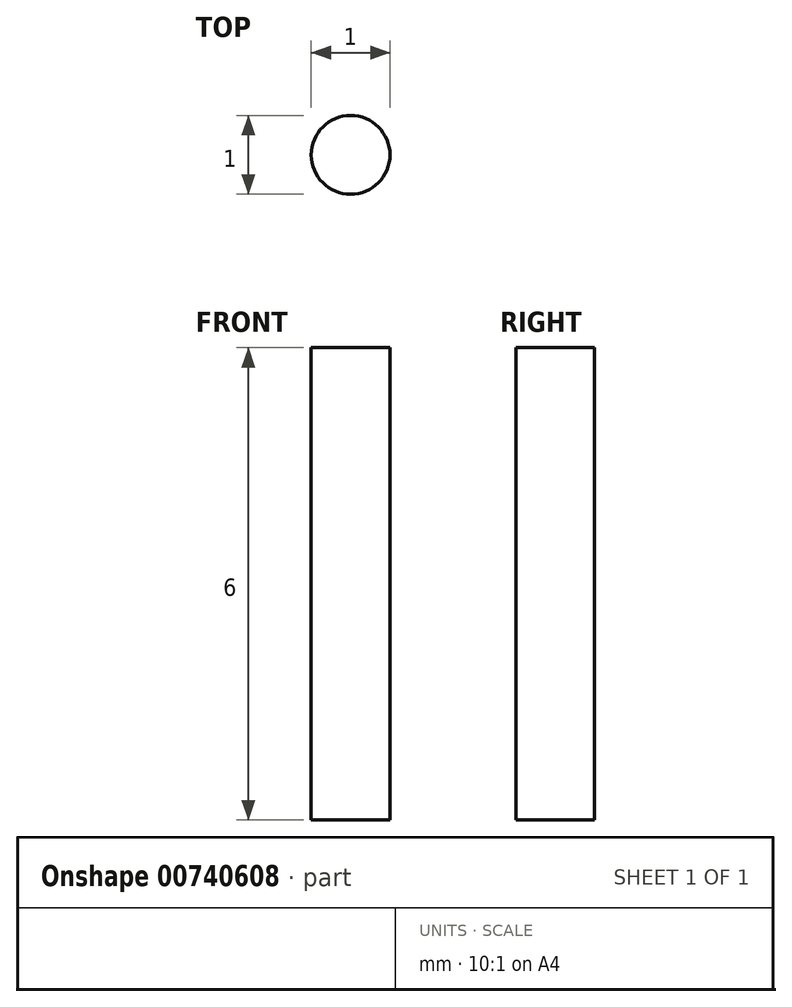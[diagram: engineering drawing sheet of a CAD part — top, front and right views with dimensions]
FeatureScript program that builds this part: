
annotation { "Feature Type Name" : "Feature", "Feature Type Description" : "" }
export const myFeature = defineFeature(function(context is Context, id is Id, definition is map)
    precondition{}
    {
        {
            var Q0;
            Q0=qCreatedBy(makeId("Top.planeOp"),FACE);
            var sketch = newSketch(context, id + "F0", { "sketchPlane" : qUnion([Q0])});
            skCircle(sketch, "E0", {"center": v(0, 0) * mm, "radius": 0.5 * mm});
            skSolve(sketch);
        }
        {
            var Q0;
            Q0=makeQuery(id+"F0.imprint","IMPRINT",FACE,{"disambiguationData":[TD([[makeQuery(id+"F0.imprint","IMPRINT",EDGE,{"derivedFrom":sQuery(id+"F0.wireOp",EDGE,"E0")}),1.0]])]});
            extrude(context, id + "F1", {"entities" : qUnion([Q0]), "depth" : 6 * mm, "offsetDistance" : 25 * mm});
        }
    });
